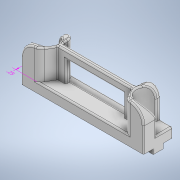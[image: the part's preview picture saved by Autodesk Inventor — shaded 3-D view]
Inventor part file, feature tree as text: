
AUTODESK INVENTOR PART (.ipt)
format: ipt  version: 2020 (Build 240168000, 168)  size: 448,000 bytes
history: native  units: in
note: dims shown in document units (in); Inventor stores cm internally (conversion verified against a paired STEP export)
features: fillet x8, sketch x6, extrude x5, other x2, hole x1
ambient origin geometry x8: Origin, YZ Plane, XZ Plane, XY Plane, X Axis, Y Axis, Z Axis, Center Point
bodies: Solid1 (feature_tree)
feature tree (22):
  other  "Annotations"
  extrude  "Extrusion1"  Depth=0.6in
  extrude  "Extrusion5"  Depth=0.1in
  extrude  "Extrusion8"  Depth=2.5in
  hole  "Hole3"  [1 undecoded]
  extrude  "Extrusion9"  Depth=0.5in
  extrude  "Extrusion10"  Depth=0.03in
  fillet  "Fillet3"  Radius=0.25in
  fillet  "Fillet4"  Radius=0.6in
  fillet  "Fillet5"  [1 undecoded]
  fillet  "Fillet6"  [1 undecoded]
  fillet  "Fillet7"  Radius=0.16in
  fillet  "Fillet8"  Radius=1.18in
  fillet  "Fillet9"  Radius=0.44in
  fillet  "Fillet10"  Radius=0.1in
  sketch  "Sketch1"  dims[d0=2.5in d1=0.6in]
  sketch  "Sketch6"  dims[d2=0.2in d3=0.0in d27=0.1in]
  sketch  "Sketch13"  dims[d28=0.2in d29=2.5in]
  sketch  "Sketch15"  dims[d30=0.2in d31=0.1in d32=0.0in]
  sketch  "Sketch16"  dims[d61=0.5in d62=0.5in]
  sketch  "Sketch18"  dims[d63=0.05in d64=0.1in d65=0.25in d66=0.6in d67=0.0in d68=60.0deg d69=120.0deg d70=0.2in d71=0.75in d72=0.4in d73=0.6in d74=0.5635in d75=1.0in d76=0.8108in d77=0.16in d78=1.18in d79=0.44in d80=0.1in d81=0.0in d89=0.12in d90=0.25in d91=0.0in d92=0.03in d93=0.03in d94=0.15in d95=0.3in d96=0.2in d97=0.03in d98=0.03in d99=0.03in d86=0.069in d87=0.3069in d88=0.25in d14=1.0in d15=1.0in d16=1.0in d17=0.15in d18=0.25in d19=0.375in d20=0.5635in d21=0.75in d22=0.8108in d23=0.0625in d24=0.75in d25=0.375in]
  other  "Linear Dimension 1"
note: 3 required parameter values undecoded (feature->parameter linkage not recoverable at this tier; creation-order binding heuristic only, values carry confidence <= 0.55)
